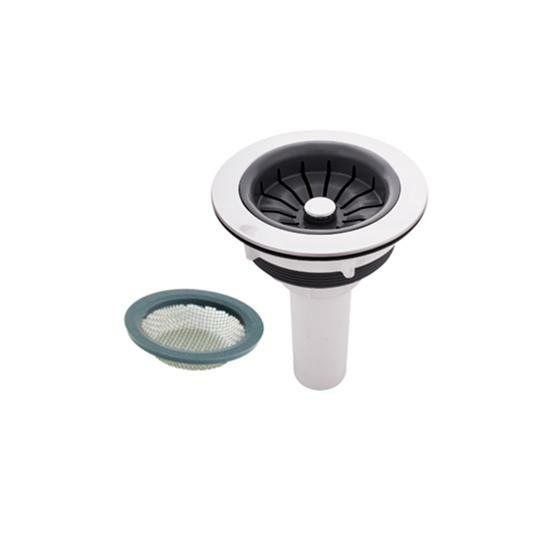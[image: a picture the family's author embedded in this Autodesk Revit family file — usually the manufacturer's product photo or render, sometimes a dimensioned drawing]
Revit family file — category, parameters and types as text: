
# Revit family: 01-19512-11 CANASTILLA ¼  INOXIDABLE PLASTICO
name_source: partatom
category: Aparatos sanitarios
revit_build: Autodesk Revit 2018 (Build: 20170223_1515(x64)
units: mm (PartAtom-declared; Revit-internal decimal feet)

## family parameters
Anfitrión = Cara
Compartido = No
Corte con vacíos al cargar = No
Cota de conector redondo = Diámetro de uso
Número OmniClass = 23.31.11.00
Punto de cálculo de habitación = No
Tipo de pieza = Normal

## types (1)
- 01-19512-11
    Alto = 156.3 mm
    Alto a Sosco = 104 mm
    Conexión AC = Sí
    Conexión AF = Sí
    Conexión de residuos = No
    Conexión de ventilación = No
    Descripción = Canastilla
    Diametro = 110 mm  [stored 0.360892 ft]
    Elevación por defecto = 0 mm  [stored 0 ft]
    Fabricante = Gricol
    Imagen de tipo = CANASTILLA ¼  INOXIDABLE PLASTICO.jpg
    Link Ficha Tecnica = https://infotecnica.gricol.com
    Metal - Acero inoxidable = Metal - Acero inoxidable
    Modelo = 01-19512-11
    Plastico - polipropileno + colorante blanco = Plastico - polipropileno + colorante blanco
    Plastico - polipropileno + colorante gris = Plastico - polipropileno + colorante gris
    Plastico ABS Cromado = Plastico ABS Cromado
    Product Name = CANASTILLA ¼  INOXIDABLE PLASTICO
    URL = https://www.gricol.com

note: [stored X ft] marks values corroborated as IEEE doubles in the binary element streams (Revit-internal decimal feet)

## geometry (parser evidence)
native form markers: Blend x2, Sweep x4
no freeform markers — native parametric forms only
